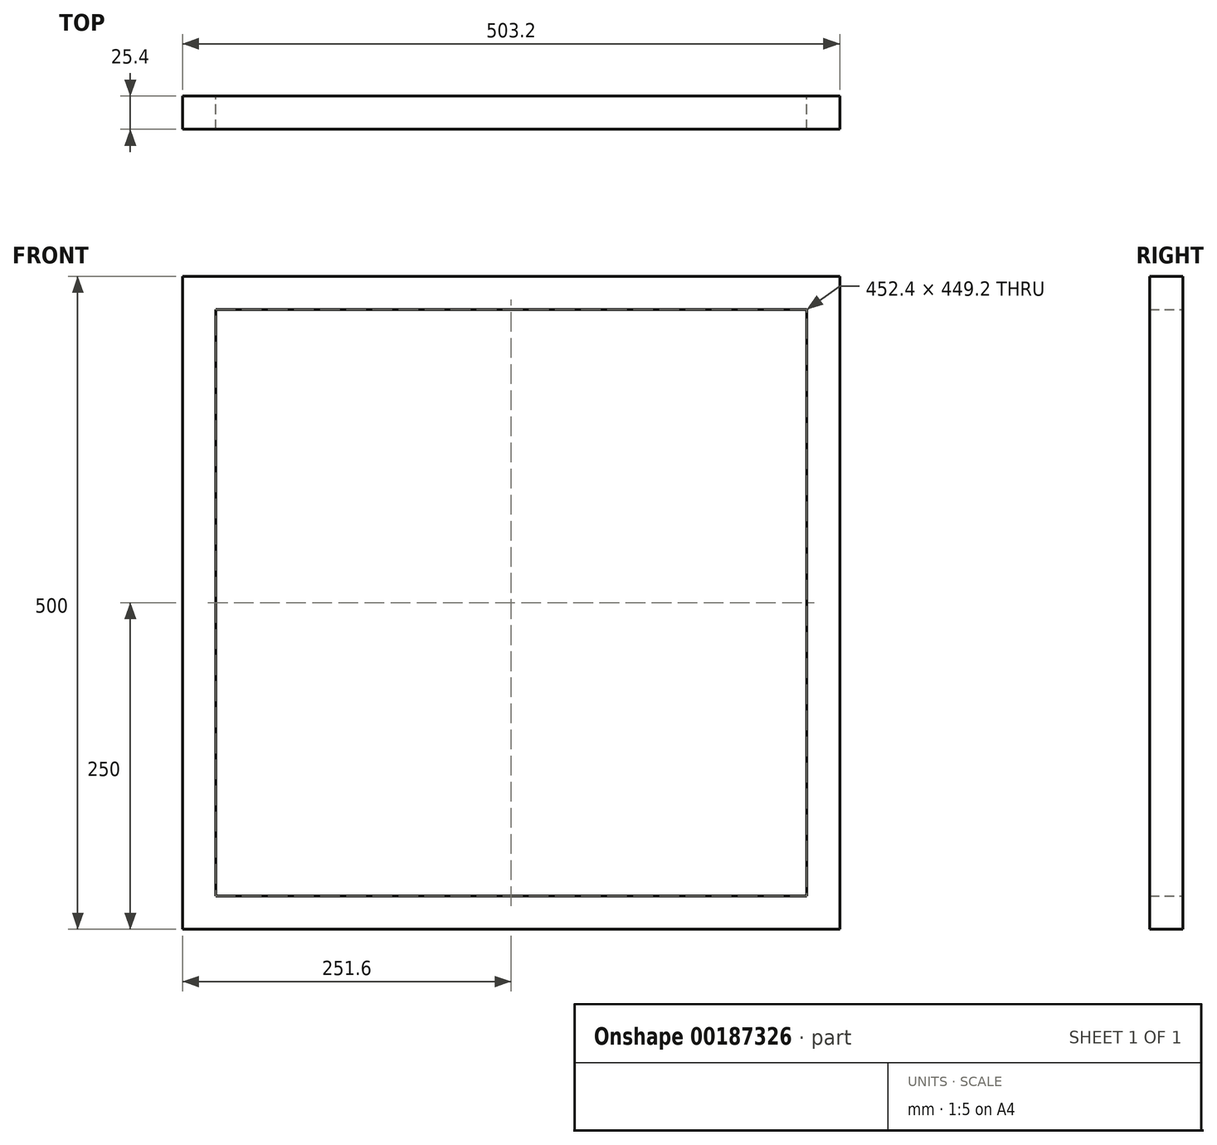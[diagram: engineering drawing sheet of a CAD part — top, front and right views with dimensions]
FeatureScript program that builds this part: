
annotation { "Feature Type Name" : "Feature", "Feature Type Description" : "" }
export const myFeature = defineFeature(function(context is Context, id is Id, definition is map)
    precondition{}
    {
        {
            var Q0;
            Q0=qCreatedBy(makeId("Front.planeOp"),FACE);
            var sketch = newSketch(context, id + "F0", { "sketchPlane" : qUnion([Q0])});
            skLineSegment(sketch, "E0.bottom", {"start": v(251.6, -250) * mm, "end": v(-251.6, -250) * mm});
            skLineSegment(sketch, "E0.top", {"start": v(251.6, 250) * mm, "end": v(-251.6, 250) * mm});
            skLineSegment(sketch, "E0.left", {"start": v(251.6, -250) * mm, "end": v(251.6, 250) * mm});
            skLineSegment(sketch, "E0.right", {"start": v(-251.6, -250) * mm, "end": v(-251.6, 250) * mm});
            skPoint(sketch, "E0.middle", {"position": v(0, 0) * mm});
            skLineSegment(sketch, "E1.0", {"start": v(-226.2, -224.6) * mm, "end": v(-226.2, 224.6) * mm});
            skLineSegment(sketch, "E1.1", {"start": v(226.2, -224.6) * mm, "end": v(-226.2, -224.6) * mm});
            skLineSegment(sketch, "E1.2", {"start": v(226.2, -224.6) * mm, "end": v(226.2, 224.6) * mm});
            skLineSegment(sketch, "E1.3", {"start": v(226.2, 224.6) * mm, "end": v(-226.2, 224.6) * mm});
            skSolve(sketch);
        }
        {
            var Q0;
            Q0 = qSketchRegion(id + "F0", true);
            extrude(context, id + "F1", {"entities" : qUnion([Q0]), "depth" : 25.4 * mm});
        }
    });
